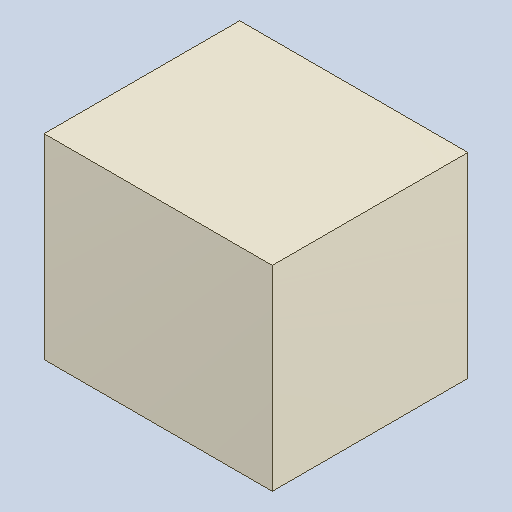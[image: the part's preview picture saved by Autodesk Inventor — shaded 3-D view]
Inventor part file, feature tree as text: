
AUTODESK INVENTOR PART (.ipt)
format: ipt  version: 2023.4 (Build 274418000, 418)  size: 82,432 bytes
history: native  units: mm
features: extrude x1
ambient origin geometry x8: Origin, YZ Plane, XZ Plane, XY Plane, X Axis, Y Axis, Z Axis, Center Point
bodies: Solid1 (feature_tree)
feature tree (1):
  extrude  "Extruded_15"  [1 undecoded]
note: 1 required parameter value undecoded (feature->parameter linkage not recoverable at this tier; creation-order binding heuristic only, values carry confidence <= 0.55)
